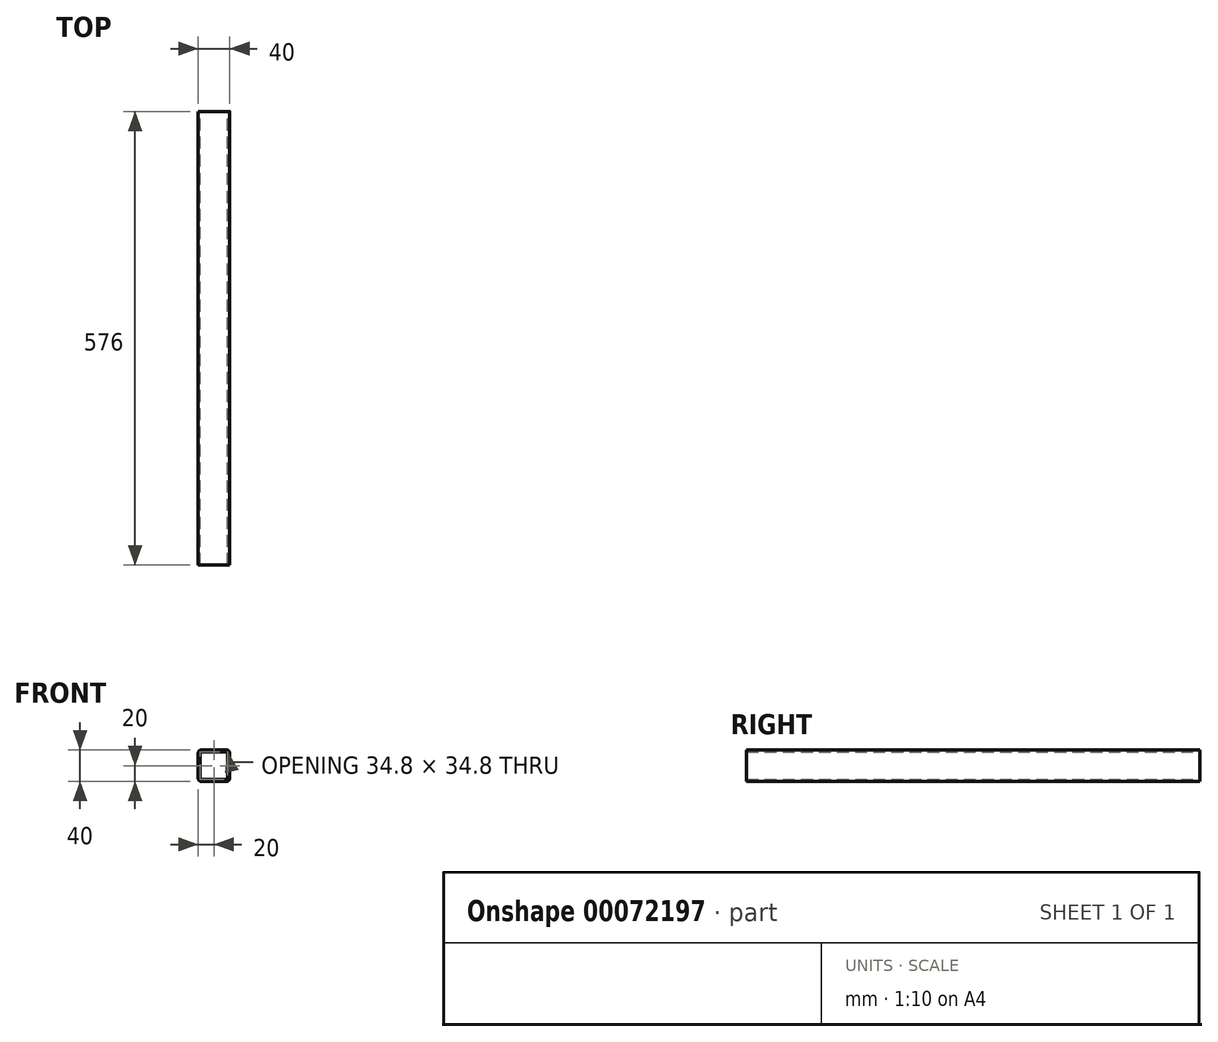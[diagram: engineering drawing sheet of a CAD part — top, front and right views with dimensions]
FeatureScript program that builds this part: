
annotation { "Feature Type Name" : "Feature", "Feature Type Description" : "" }
export const myFeature = defineFeature(function(context is Context, id is Id, definition is map)
    precondition{}
    {
        {
            var Q0;
            Q0=qCreatedBy(makeId("Front.planeOp"),FACE);
            var sketch = newSketch(context, id + "F0", { "sketchPlane" : qUnion([Q0])});
            skLineSegment(sketch, "E0.bottom", {"start": v(-20, 20) * mm, "end": v(20, 20) * mm});
            skLineSegment(sketch, "E0.top", {"start": v(-20, -20) * mm, "end": v(20, -20) * mm});
            skLineSegment(sketch, "E0.left", {"start": v(-20, 20) * mm, "end": v(-20, -20) * mm});
            skLineSegment(sketch, "E0.right", {"start": v(20, 20) * mm, "end": v(20, -20) * mm});
            skLineSegment(sketch, "E1.0", {"start": v(-17.4, 17.4) * mm, "end": v(17.4, 17.4) * mm});
            skLineSegment(sketch, "E1.1", {"start": v(-17.4, 17.4) * mm, "end": v(-17.4, -17.4) * mm});
            skLineSegment(sketch, "E1.2", {"start": v(-17.4, -17.4) * mm, "end": v(17.4, -17.4) * mm});
            skLineSegment(sketch, "E1.3", {"start": v(17.4, 17.4) * mm, "end": v(17.4, -17.4) * mm});
            skSolve(sketch);
        }
        {
            var Q0;
            Q0=makeQuery(id+"F0.imprint","IMPRINT",FACE,{"disambiguationData":[TD([[makeQuery(id+"F0.imprint","IMPRINT",EDGE,{"derivedFrom":sQuery(id+"F0.wireOp",EDGE,"E0.bottom")}),-1.0]])]});
            extrude(context, id + "F1", {"entities" : qUnion([Q0]), "depth" : 576 * mm});
        }
        {
            var Q0;
            Q0=makeQuery(id+"F1.opExtrude","SWEPT_EDGE",EDGE,{"disambiguationData":[OSD([sQuery(id+"F0.wireOp",EDGE,"E0.bottom"),sQuery(id+"F0.wireOp",EDGE,"E0.right")])]});
            var Q1;
            Q1=makeQuery(id+"F1.opExtrude","SWEPT_EDGE",EDGE,{"disambiguationData":[OSD([sQuery(id+"F0.wireOp",EDGE,"E0.bottom"),sQuery(id+"F0.wireOp",EDGE,"E0.left")])]});
            var Q2;
            Q2=makeQuery(id+"F1.opExtrude","SWEPT_EDGE",EDGE,{"disambiguationData":[OSD([sQuery(id+"F0.wireOp",EDGE,"E0.top"),sQuery(id+"F0.wireOp",EDGE,"E0.right")])]});
            var Q3;
            Q3=makeQuery(id+"F1.opExtrude","SWEPT_EDGE",EDGE,{"disambiguationData":[OSD([sQuery(id+"F0.wireOp",EDGE,"E0.top"),sQuery(id+"F0.wireOp",EDGE,"E0.left")])]});
            fillet(context, id + "F2", {"entities" : qUnion([Q0, Q1, Q2, Q3]), "radius" : 4 * mm, "tangentPropagation" : true, "allowEdgeOverflow" : false});
        }
        {
            var Q0;
            Q0=makeQuery(id+"F1.opExtrude","SWEPT_EDGE",EDGE,{"disambiguationData":[OSD([sQuery(id+"F0.wireOp",EDGE,"E1.0"),sQuery(id+"F0.wireOp",EDGE,"E1.1")])]});
            var Q1;
            Q1=makeQuery(id+"F1.opExtrude","SWEPT_EDGE",EDGE,{"disambiguationData":[OSD([sQuery(id+"F0.wireOp",EDGE,"E1.1"),sQuery(id+"F0.wireOp",EDGE,"E1.2")])]});
            var Q2;
            Q2=makeQuery(id+"F1.opExtrude","SWEPT_EDGE",EDGE,{"disambiguationData":[OSD([sQuery(id+"F0.wireOp",EDGE,"E1.2"),sQuery(id+"F0.wireOp",EDGE,"E1.3")])]});
            var Q3;
            Q3=makeQuery(id+"F1.opExtrude","SWEPT_EDGE",EDGE,{"disambiguationData":[OSD([sQuery(id+"F0.wireOp",EDGE,"E1.0"),sQuery(id+"F0.wireOp",EDGE,"E1.3")])]});
            fillet(context, id + "F3", {"entities" : qUnion([Q0, Q1, Q2, Q3]), "radius" : 2 * mm, "tangentPropagation" : true, "allowEdgeOverflow" : false});
        }
    });
